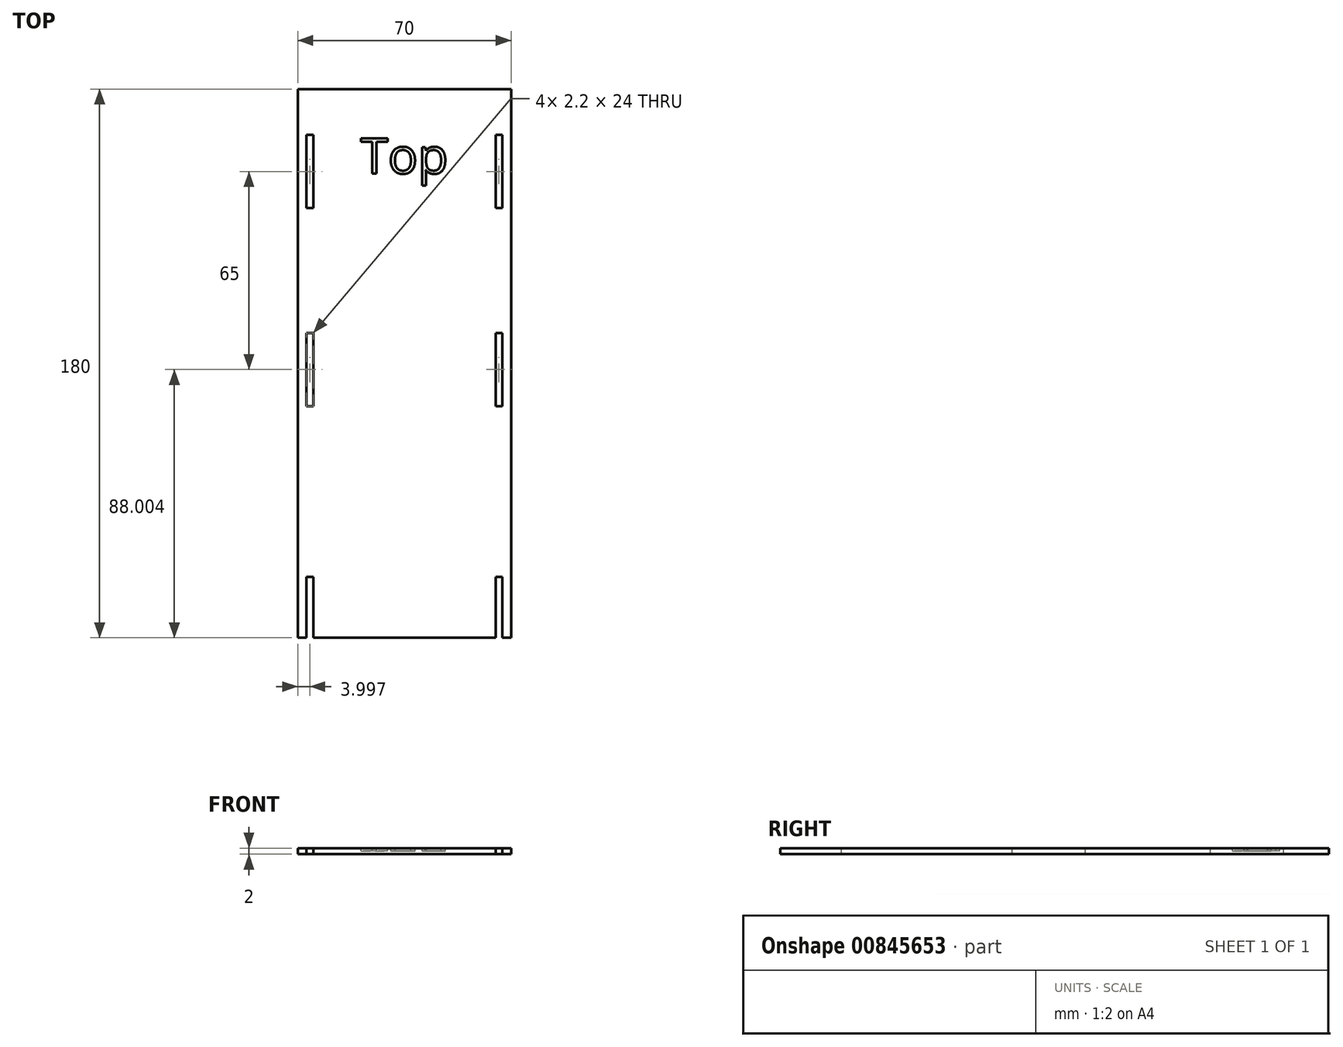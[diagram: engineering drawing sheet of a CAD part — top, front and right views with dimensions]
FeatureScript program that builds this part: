
annotation { "Feature Type Name" : "Feature", "Feature Type Description" : "" }
export const myFeature = defineFeature(function(context is Context, id is Id, definition is map)
    precondition{}
    {
        {
            var Q0;
            Q0=qCreatedBy(makeId("Top.planeOp"),FACE);
            var sketch = newSketch(context, id + "F0", { "sketchPlane" : qUnion([Q0])});
            skLineSegment(sketch, "E0.bottom", {"start": v(-35.7, 89.27) * mm, "end": v(34.3, 89.27) * mm});
            skLineSegment(sketch, "E0.top", {"start": v(-35.7, -90.73) * mm, "end": v(34.3, -90.73) * mm});
            skLineSegment(sketch, "E0.left", {"start": v(-35.7, 89.27) * mm, "end": v(-35.7, -90.73) * mm});
            skLineSegment(sketch, "E0.right", {"start": v(34.3, 89.27) * mm, "end": v(34.3, -90.73) * mm});
            skSolve(sketch);
        }
        {
            var Q0;
            Q0=makeQuery(id+"F0.imprint","IMPRINT",FACE,{"disambiguationData":[TD([[makeQuery(id+"F0.imprint","IMPRINT",EDGE,{"derivedFrom":sQuery(id+"F0.wireOp",EDGE,"E0.bottom")}),-1.0]])]});
            var Q1;
            Q1 = qSketchRegion(id + "F2", true);
            extrude(context, id + "F1", {"entities" : qUnion([Q0, Q1]), "depth" : 2 * mm, "offsetDistance" : 25 * mm});
        }
        {
            var Q0;
            Q0=qCreatedBy(makeId("Top.planeOp"),FACE);
            var sketch = newSketch(context, id + "F2", { "sketchPlane" : qUnion([Q0])});
            skLineSegment(sketch, "E1", {"start": v(-56.72, 74.27) * mm, "end": v(93.74, 74.27) * mm, "construction": true});
            skLineSegment(sketch, "E2", {"start": v(-61.51, -14.73) * mm, "end": v(81.1, -14.73) * mm, "construction": true});
            skLineSegment(sketch, "E3", {"start": v(-64.34, -70.73) * mm, "end": v(85.68, -70.73) * mm, "construction": true});
            skLineSegment(sketch, "E4", {"start": v(-56.72, 9.27) * mm, "end": v(82.2, 9.27) * mm, "construction": true});
            skLineSegment(sketch, "E5", {"start": v(-58.03, 50.27) * mm, "end": v(80.24, 50.27) * mm, "construction": true});
            skLineSegment(sketch, "E6", {"start": v(-59.55, -94.73) * mm, "end": v(92, -94.73) * mm, "construction": true});
            skLineSegment(sketch, "E7", {"start": v(29.2, -110.05) * mm, "end": v(29.2, 99.35) * mm, "construction": true});
            skLineSegment(sketch, "E8", {"start": v(-32.8, 99.35) * mm, "end": v(-32.8, -122.98) * mm, "construction": true});
            skLineSegment(sketch, "E9", {"start": v(-30.6, 105.5) * mm, "end": v(-30.6, -133.14) * mm, "construction": true});
            skLineSegment(sketch, "E10", {"start": v(31.4, 105.5) * mm, "end": v(31.4, -137.76) * mm, "construction": true});
            skLineSegment(sketch, "E11.bottom", {"start": v(-32.8, 74.27) * mm, "end": v(-30.6, 74.27) * mm});
            skLineSegment(sketch, "E11.top", {"start": v(-32.8, 50.27) * mm, "end": v(-30.6, 50.27) * mm});
            skLineSegment(sketch, "E11.left", {"start": v(-32.8, 74.27) * mm, "end": v(-32.8, 50.27) * mm});
            skLineSegment(sketch, "E11.right", {"start": v(-30.6, 74.27) * mm, "end": v(-30.6, 50.27) * mm});
            skLineSegment(sketch, "E12.bottom", {"start": v(29.2, 74.27) * mm, "end": v(31.4, 74.27) * mm});
            skLineSegment(sketch, "E12.top", {"start": v(29.2, 50.27) * mm, "end": v(31.4, 50.27) * mm});
            skLineSegment(sketch, "E12.left", {"start": v(29.2, 74.27) * mm, "end": v(29.2, 50.27) * mm});
            skLineSegment(sketch, "E12.right", {"start": v(31.4, 74.27) * mm, "end": v(31.4, 50.27) * mm});
            skLineSegment(sketch, "E13.bottom", {"start": v(-32.8, 9.27) * mm, "end": v(-30.6, 9.27) * mm});
            skLineSegment(sketch, "E13.top", {"start": v(-32.8, -14.73) * mm, "end": v(-30.6, -14.73) * mm});
            skLineSegment(sketch, "E13.left", {"start": v(-32.8, 9.27) * mm, "end": v(-32.8, -14.73) * mm});
            skLineSegment(sketch, "E13.right", {"start": v(-30.6, 9.27) * mm, "end": v(-30.6, -14.73) * mm});
            skLineSegment(sketch, "E14.bottom", {"start": v(29.2, 9.27) * mm, "end": v(31.4, 9.27) * mm});
            skLineSegment(sketch, "E14.top", {"start": v(29.2, -14.73) * mm, "end": v(31.4, -14.73) * mm});
            skLineSegment(sketch, "E14.left", {"start": v(29.2, 9.27) * mm, "end": v(29.2, -14.73) * mm});
            skLineSegment(sketch, "E14.right", {"start": v(31.4, 9.27) * mm, "end": v(31.4, -14.73) * mm});
            skLineSegment(sketch, "E15.bottom", {"start": v(-32.8, -70.73) * mm, "end": v(-30.6, -70.73) * mm});
            skLineSegment(sketch, "E15.top", {"start": v(-32.8, -94.73) * mm, "end": v(-30.6, -94.73) * mm});
            skLineSegment(sketch, "E15.left", {"start": v(-32.8, -70.73) * mm, "end": v(-32.8, -94.73) * mm});
            skLineSegment(sketch, "E15.right", {"start": v(-30.6, -70.73) * mm, "end": v(-30.6, -94.73) * mm});
            skLineSegment(sketch, "E16.bottom", {"start": v(29.2, -70.73) * mm, "end": v(31.4, -70.73) * mm});
            skLineSegment(sketch, "E16.top", {"start": v(29.2, -94.73) * mm, "end": v(31.4, -94.73) * mm});
            skLineSegment(sketch, "E16.left", {"start": v(29.2, -70.73) * mm, "end": v(29.2, -94.73) * mm});
            skLineSegment(sketch, "E16.right", {"start": v(31.4, -70.73) * mm, "end": v(31.4, -94.73) * mm});
            skSolve(sketch);
        }
        {
            var Q0;
            Q0 = qSketchRegion(id + "F2", true);
            extrude(context, id + "F3", {"entities" : qUnion([Q0]), "operationType" : NewBodyOperationType.REMOVE, "depth" : 25 * mm, "offsetDistance" : 25 * mm});
        }
        {
            var Q0;
            Q0=makeQuery(id+"F1.opExtrude","CAP_FACE",FACE,{"disambiguationData":[OSD([sQuery(id+"F0.wireOp",EDGE,"E0.bottom"),sQuery(id+"F0.wireOp",EDGE,"E0.top"),sQuery(id+"F0.wireOp",EDGE,"E0.left"),sQuery(id+"F0.wireOp",EDGE,"E0.right")])],"isStart":false});
            var sketch = newSketch(context, id + "F4", { "sketchPlane" : qUnion([Q0])});
            skText(sketch, "E17", { "text": "Top", "fontName": "OpenSans-Regular.ttf"});
            const initialGuessF4  = {"E17": [-0.01502, 0.06158, 1, 0, 0.01165]};
            skSetInitialGuess(sketch, initialGuessF4);
            skSolve(sketch);
        }
        {
            var Q0;
            Q0 = qSketchRegion(id + "F4", true);
            extrude(context, id + "F5", {"entities" : qUnion([Q0]), "operationType" : NewBodyOperationType.REMOVE, "oppositeDirection" : true, "depth" : 1 * mm, "offsetDistance" : 25 * mm});
        }
    });
